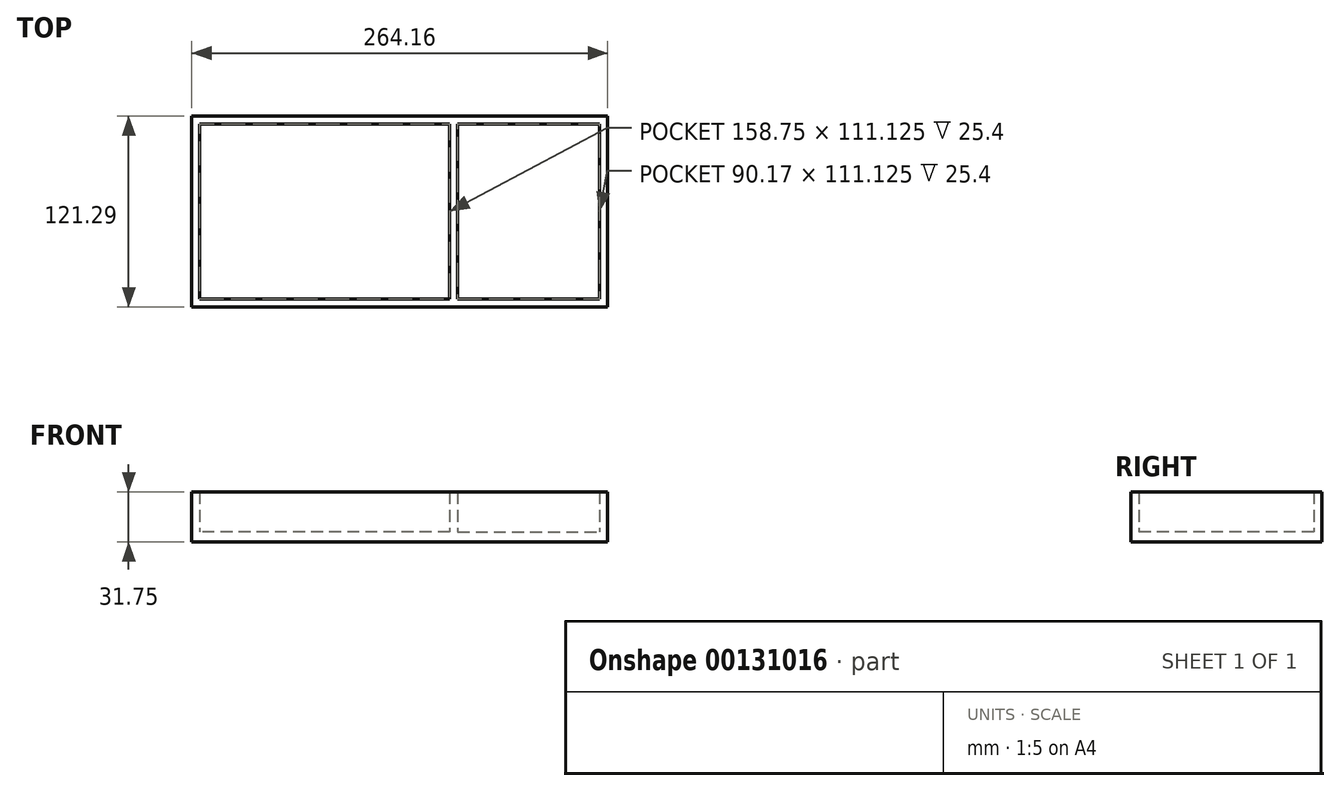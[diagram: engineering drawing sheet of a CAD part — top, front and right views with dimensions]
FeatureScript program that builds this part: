
annotation { "Feature Type Name" : "Feature", "Feature Type Description" : "" }
export const myFeature = defineFeature(function(context is Context, id is Id, definition is map)
    precondition{}
    {
        {
            var Q0;
            Q0=qCreatedBy(makeId("Top.planeOp"),FACE);
            var sketch = newSketch(context, id + "F0", { "sketchPlane" : qUnion([Q0])});
            skLineSegment(sketch, "E0.bottom", {"start": v(-128.08, 69.77) * mm, "end": v(136.08, 69.77) * mm});
            skLineSegment(sketch, "E0.top", {"start": v(-128.08, -51.52) * mm, "end": v(136.08, -51.52) * mm});
            skLineSegment(sketch, "E0.left", {"start": v(-128.08, 69.77) * mm, "end": v(-128.08, -51.52) * mm});
            skLineSegment(sketch, "E0.right", {"start": v(136.08, 69.77) * mm, "end": v(136.08, -51.52) * mm});
            skLineSegment(sketch, "E1.0", {"start": v(-123, 64.69) * mm, "end": v(-123, -46.44) * mm});
            skLineSegment(sketch, "E1.2", {"start": v(131, 64.69) * mm, "end": v(131, -46.44) * mm});
            skPoint(sketch, "E2", {"position": v(35.75, 64.69) * mm});
            skLineSegment(sketch, "E3", {"start": v(35.75, 64.69) * mm, "end": v(35.75, -46.44) * mm});
            skLineSegment(sketch, "E4.0", {"start": v(40.83, 64.69) * mm, "end": v(40.83, -46.44) * mm});
            skLineSegment(sketch, "E5", {"start": v(40.83, -46.44) * mm, "end": v(131, -46.44) * mm});
            skLineSegment(sketch, "E6", {"start": v(35.75, -46.44) * mm, "end": v(-123, -46.44) * mm});
            skLineSegment(sketch, "E7", {"start": v(-123, 64.69) * mm, "end": v(35.75, 64.69) * mm});
            skLineSegment(sketch, "E8", {"start": v(40.83, 64.69) * mm, "end": v(131, 64.69) * mm});
            skSolve(sketch);
        }
        {
            var Q0;
            Q0=makeQuery(id+"F0.imprint","IMPRINT",FACE,{"disambiguationData":[TD([[makeQuery(id+"F0.imprint","IMPRINT",EDGE,{"derivedFrom":sQuery(id+"F0.wireOp",EDGE,"E0.bottom")}),-1.0]])]});
            extrude(context, id + "F1", {"entities" : qUnion([Q0]), "depth" : 31.75 * mm});
        }
        {
            var Q0;
            Q0=makeQuery(id+"F0.imprint","IMPRINT",FACE,{"disambiguationData":[TD([[makeQuery(id+"F0.imprint","IMPRINT",EDGE,{"derivedFrom":sQuery(id+"F0.wireOp",EDGE,"E1.0")}),1.0]])]});
            var Q1;
            Q1=makeQuery(id+"F0.imprint","IMPRINT",FACE,{"disambiguationData":[TD([[makeQuery(id+"F0.imprint","IMPRINT",EDGE,{"derivedFrom":sQuery(id+"F0.wireOp",EDGE,"E1.2")}),-1.0]])]});
            extrude(context, id + "F2", {"entities" : qUnion([Q0, Q1]), "operationType" : NewBodyOperationType.ADD, "depth" : 6.35 * mm});
        }
    });
